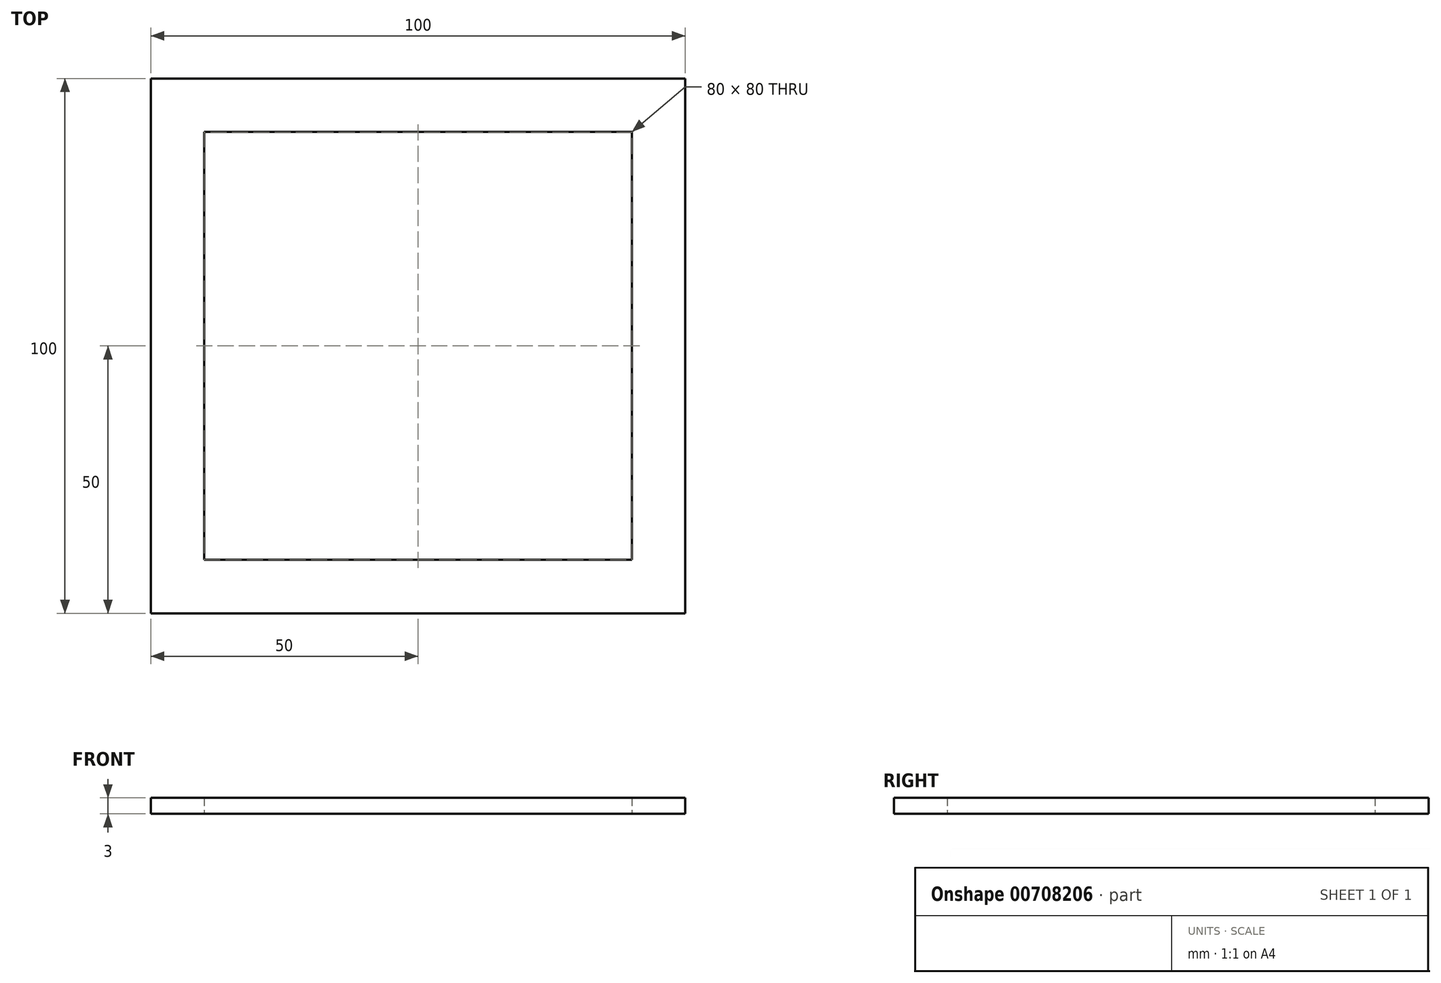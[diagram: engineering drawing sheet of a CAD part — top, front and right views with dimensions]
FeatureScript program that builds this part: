
annotation { "Feature Type Name" : "Feature", "Feature Type Description" : "" }
export const myFeature = defineFeature(function(context is Context, id is Id, definition is map)
    precondition{}
    {
        {
            var Q0;
            Q0=qCreatedBy(makeId("Top.planeOp"),FACE);
            var sketch = newSketch(context, id + "F0", { "sketchPlane" : qUnion([Q0])});
            skLineSegment(sketch, "E0.bottom", {"start": v(0, 0) * mm, "end": v(100, 0) * mm});
            skLineSegment(sketch, "E0.top", {"start": v(0, -100) * mm, "end": v(100, -100) * mm});
            skLineSegment(sketch, "E0.left", {"start": v(0, 0) * mm, "end": v(0, -100) * mm});
            skLineSegment(sketch, "E0.right", {"start": v(100, 0) * mm, "end": v(100, -100) * mm});
            skLineSegment(sketch, "E1.bottom", {"start": v(10, -10) * mm, "end": v(90, -10) * mm});
            skLineSegment(sketch, "E1.top", {"start": v(10, -90) * mm, "end": v(90, -90) * mm});
            skLineSegment(sketch, "E1.left", {"start": v(10, -10) * mm, "end": v(10, -90) * mm});
            skLineSegment(sketch, "E1.right", {"start": v(90, -10) * mm, "end": v(90, -90) * mm});
            skSolve(sketch);
        }
        {
            var Q0;
            Q0=makeQuery(id+"F0.imprint","IMPRINT",FACE,{"disambiguationData":[TD([[makeQuery(id+"F0.imprint","IMPRINT",EDGE,{"derivedFrom":sQuery(id+"F0.wireOp",EDGE,"E0.bottom")}),-1.0]])]});
            extrude(context, id + "F1", {"entities" : qUnion([Q0]), "depth" : 3 * mm, "offsetDistance" : 25 * mm});
        }
    });
